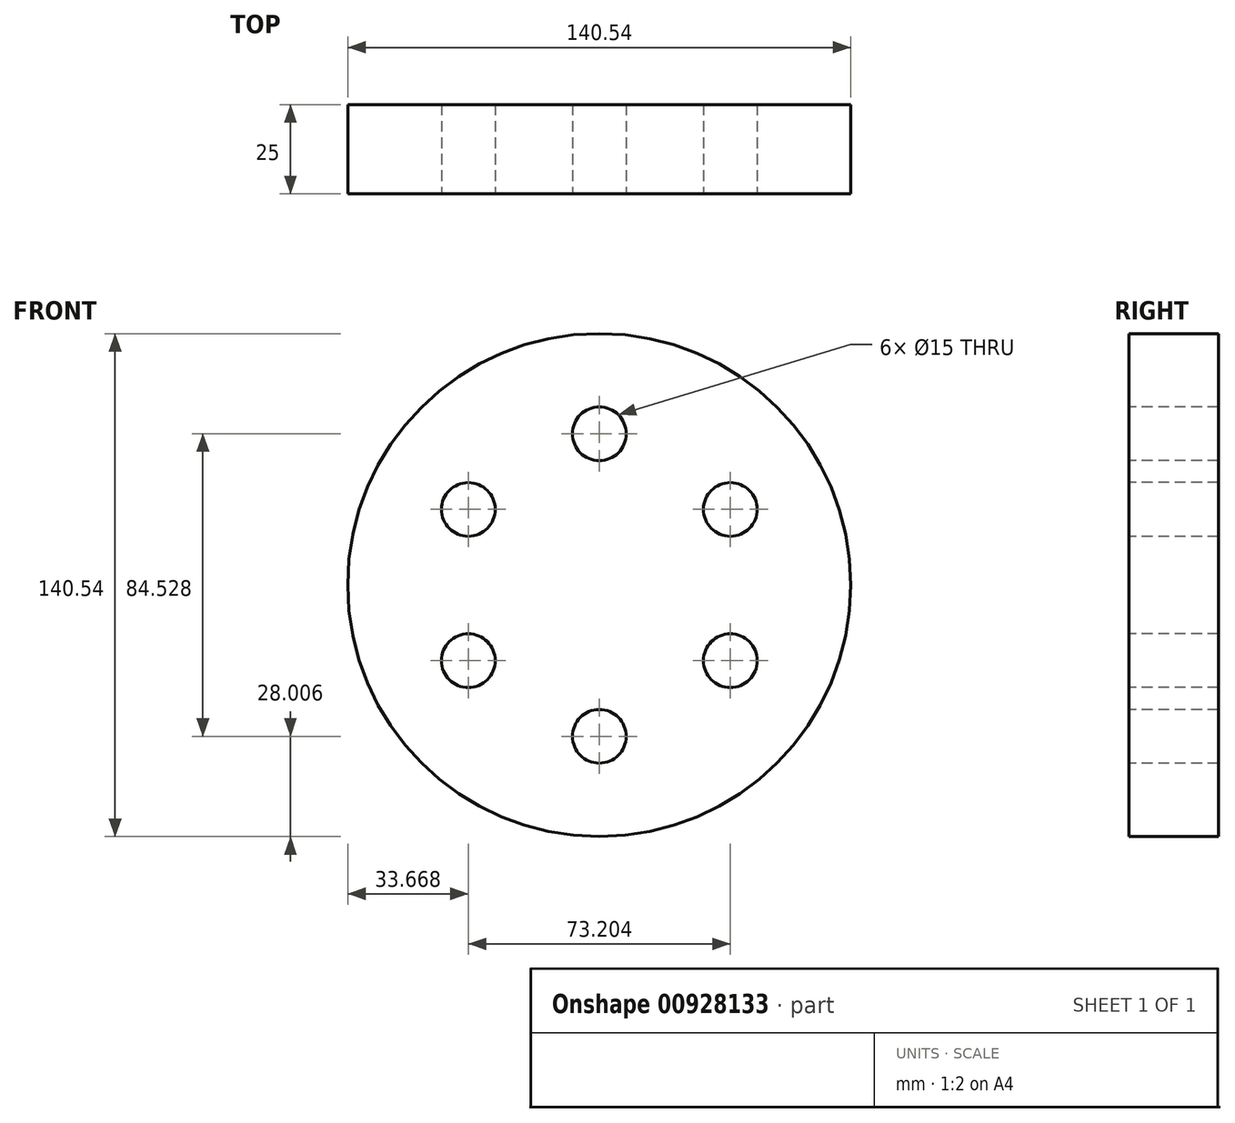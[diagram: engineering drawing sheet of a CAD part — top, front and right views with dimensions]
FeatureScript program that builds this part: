
annotation { "Feature Type Name" : "Feature", "Feature Type Description" : "" }
export const myFeature = defineFeature(function(context is Context, id is Id, definition is map)
    precondition{}
    {
        {
            var Q0;
            Q0=qCreatedBy(makeId("Front.planeOp"),FACE);
            var sketch = newSketch(context, id + "F0", { "sketchPlane" : qUnion([Q0])});
            skCircle(sketch, "E0", {"center": v(0, 0) * mm, "radius": 70.27 * mm});
            skSolve(sketch);
        }
        {
            var Q0;
            Q0 = qSketchRegion(id + "F0", true);
            extrude(context, id + "F1", {"entities" : qUnion([Q0]), "depth" : 25 * mm, "offsetDistance" : 25 * mm});
        }
        {
            var Q0;
            Q0=makeQuery(id+"F1.opExtrude","CAP_FACE",FACE,{"disambiguationData":[OSD([sQuery(id+"F0.wireOp",EDGE,"E0")])],"isStart":false});
            var sketch = newSketch(context, id + "F2", { "sketchPlane" : qUnion([Q0])});
            skCircle(sketch, "E1", {"center": v(0, 42.26) * mm, "radius": 7.5 * mm});
            skCircle(sketch, "E2.1.0", {"center": v(-36.6, 21.13) * mm, "radius": 7.5 * mm});
            skCircle(sketch, "E2.2.0", {"center": v(-36.6, -21.13) * mm, "radius": 7.5 * mm});
            skCircle(sketch, "E2.3.0", {"center": v(0, -42.26) * mm, "radius": 7.5 * mm});
            skPoint(sketch, "E2.center", {"position": v(0, 0) * mm});
            skCircle(sketch, "E3.1.4.0", {"center": v(36.6, -21.13) * mm, "radius": 7.5 * mm});
            skCircle(sketch, "E3.1.5.0", {"center": v(36.6, 21.13) * mm, "radius": 7.5 * mm});
            skSolve(sketch);
        }
        {
            var Q0;
            Q0 = qSketchRegion(id + "F2", true);
            extrude(context, id + "F3", {"entities" : qUnion([Q0]), "operationType" : NewBodyOperationType.REMOVE, "oppositeDirection" : true, "depth" : 25 * mm, "offsetDistance" : 25 * mm});
        }
    });
